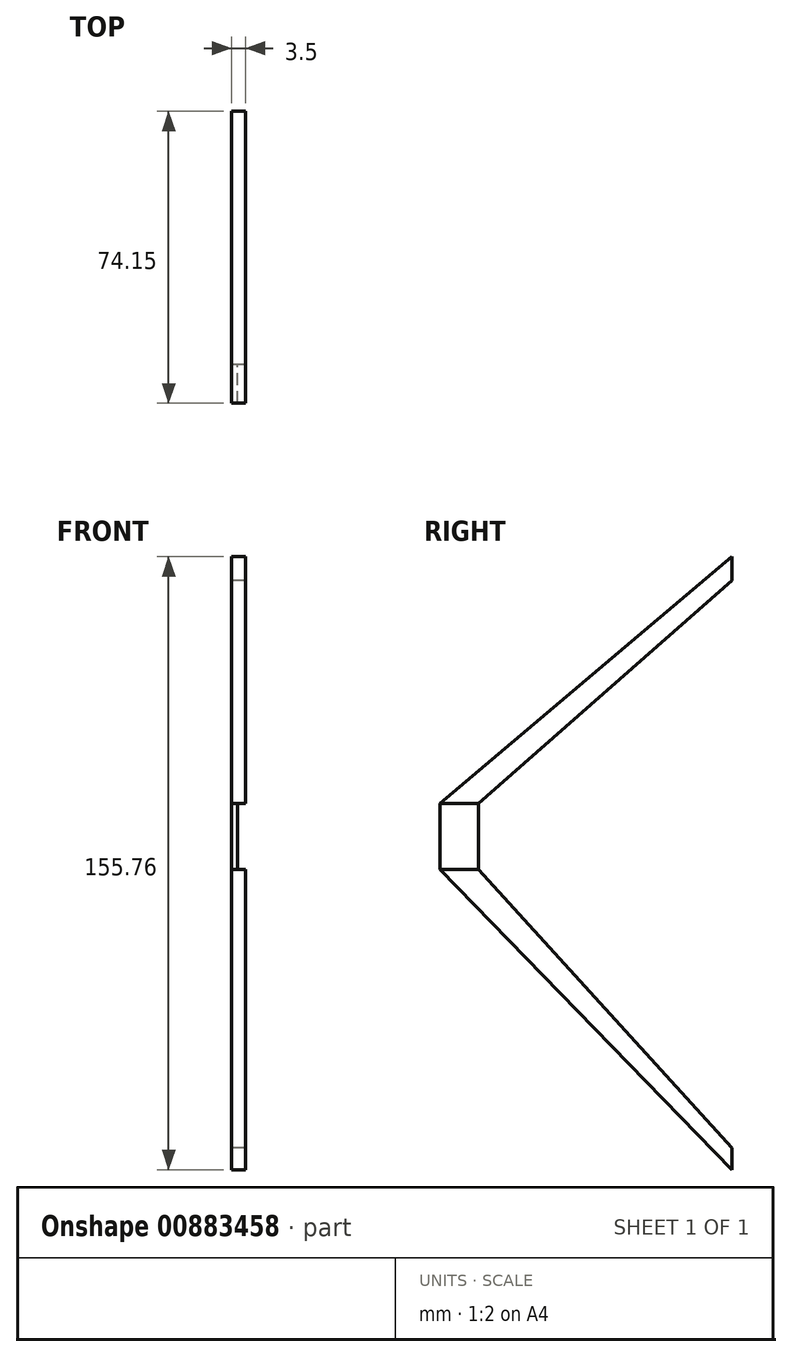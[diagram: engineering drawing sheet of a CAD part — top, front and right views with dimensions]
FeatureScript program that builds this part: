
annotation { "Feature Type Name" : "Feature", "Feature Type Description" : "" }
export const myFeature = defineFeature(function(context is Context, id is Id, definition is map)
    precondition{}
    {
        {
            var Q0;
            Q0=qCreatedBy(makeId("Right.planeOp"),FACE);
            var sketch = newSketch(context, id + "F0", { "sketchPlane" : qUnion([Q0])});
            skLineSegment(sketch, "E0", {"start": v(0, 79.42) * mm, "end": v(0, 73.28) * mm});
            skLineSegment(sketch, "E1", {"start": v(0, 73.28) * mm, "end": v(-64.4, 16.65) * mm});
            skLineSegment(sketch, "E2", {"start": v(-64.4, 16.65) * mm, "end": v(-74.15, 16.65) * mm});
            skLineSegment(sketch, "E3", {"start": v(-74.15, 16.65) * mm, "end": v(0, 79.42) * mm});
            skLineSegment(sketch, "E4", {"start": v(-74.15, 16.65) * mm, "end": v(-74.15, 0) * mm});
            skLineSegment(sketch, "E5", {"start": v(-74.15, 0) * mm, "end": v(-64.4, 0) * mm});
            skLineSegment(sketch, "E6", {"start": v(-64.4, 0) * mm, "end": v(-64.4, 16.65) * mm});
            skLineSegment(sketch, "E7", {"start": v(-64.4, 0) * mm, "end": v(0, -70.85) * mm});
            skLineSegment(sketch, "E8", {"start": v(0, -70.85) * mm, "end": v(0, -76.34) * mm});
            skLineSegment(sketch, "E9", {"start": v(0, -76.34) * mm, "end": v(-74.15, 0) * mm});
            skSolve(sketch);
        }
        {
            var Q0;
            Q0=makeQuery(id+"F0.imprint","IMPRINT",FACE,{"disambiguationData":[TD([[makeQuery(id+"F0.imprint","IMPRINT",EDGE,{"derivedFrom":sQuery(id+"F0.wireOp",EDGE,"E0")}),-1.0]])]});
            var Q1;
            Q1=makeQuery(id+"F0.imprint","IMPRINT",FACE,{"disambiguationData":[TD([[makeQuery(id+"F0.imprint","IMPRINT",EDGE,{"derivedFrom":sQuery(id+"F0.wireOp",EDGE,"E5")}),-1.0]])]});
            var Q2;
            Q2=makeQuery(id+"F0.imprint","IMPRINT",FACE,{"disambiguationData":[TD([[makeQuery(id+"F0.imprint","IMPRINT",EDGE,{"derivedFrom":sQuery(id+"F0.wireOp",EDGE,"E2")}),1.0]])]});
            extrude(context, id + "F1", {"entities" : qUnion([Q0, Q1, Q2]), "depth" : 1.5 * mm, "offsetDistance" : 25.4 * mm});
        }
        {
            var Q0;
            Q0=makeQuery(id+"F1.opExtrude","CAP_FACE",FACE,{"disambiguationData":[OSD([sQuery(id+"F0.wireOp",EDGE,"E0"),sQuery(id+"F0.wireOp",EDGE,"E1"),sQuery(id+"F0.wireOp",EDGE,"E3"),sQuery(id+"F0.wireOp",EDGE,"E4"),sQuery(id+"F0.wireOp",EDGE,"E6"),sQuery(id+"F0.wireOp",EDGE,"E7"),sQuery(id+"F0.wireOp",EDGE,"E8"),sQuery(id+"F0.wireOp",EDGE,"E9")])],"isStart":false});
            var sketch = newSketch(context, id + "F2", { "sketchPlane" : qUnion([Q0])});
            skLineSegment(sketch, "E10", {"start": v(-74.15, 16.65) * mm, "end": v(-64.4, 16.65) * mm});
            skLineSegment(sketch, "E11", {"start": v(-64.4, 16.65) * mm, "end": v(0, 73.28) * mm});
            skLineSegment(sketch, "E12", {"start": v(0, 73.28) * mm, "end": v(0, 79.42) * mm});
            skLineSegment(sketch, "E13", {"start": v(0, 79.42) * mm, "end": v(-74.15, 16.65) * mm});
            skLineSegment(sketch, "E14", {"start": v(-74.15, 0) * mm, "end": v(-64.4, 0) * mm});
            skLineSegment(sketch, "E15", {"start": v(-64.4, 0) * mm, "end": v(0, -70.85) * mm});
            skLineSegment(sketch, "E16", {"start": v(0, -70.85) * mm, "end": v(0, -76.34) * mm});
            skLineSegment(sketch, "E17", {"start": v(0, -76.34) * mm, "end": v(-74.15, 0) * mm});
            skSolve(sketch);
        }
        {
            var Q0;
            Q0=makeQuery(id+"F2.imprint","IMPRINT",FACE,{"disambiguationData":[TD([[makeQuery(id+"F2.imprint","IMPRINT",EDGE,{"derivedFrom":sQuery(id+"F2.wireOp",EDGE,"E10")}),1.0]])]});
            var Q1;
            Q1=makeQuery(id+"F2.imprint","IMPRINT",FACE,{"disambiguationData":[TD([[makeQuery(id+"F2.imprint","IMPRINT",EDGE,{"derivedFrom":sQuery(id+"F2.wireOp",EDGE,"E14")}),-1.0]])]});
            extrude(context, id + "F3", {"entities" : qUnion([Q0, Q1]), "operationType" : NewBodyOperationType.ADD, "depth" : 2 * mm, "offsetDistance" : 25 * mm});
        }
    });
